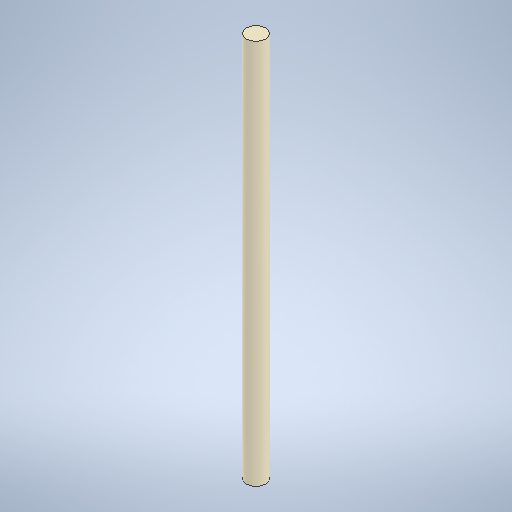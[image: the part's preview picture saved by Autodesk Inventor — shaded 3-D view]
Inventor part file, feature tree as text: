
AUTODESK INVENTOR PART (.ipt)
format: ipt  version: 2025.2 (Build 292293000, 293)  size: 233,472 bytes
history: native  units: in
note: dims shown in document units (in); Inventor stores cm internally (conversion verified against a paired STEP export)
features: extrude x1, sketch x1
ambient origin geometry x8: Origin, YZ Plane, XZ Plane, XY Plane, X Axis, Y Axis, Z Axis, Center Point
bodies: Solid1 (feature_tree)
feature tree (2):
  extrude  "Extrusion1"  Depth=10.0in TaperAngle=0.0deg
  sketch  "Sketch1"  dims[d0=0.5in d1=10.0in d2=0.0in]
